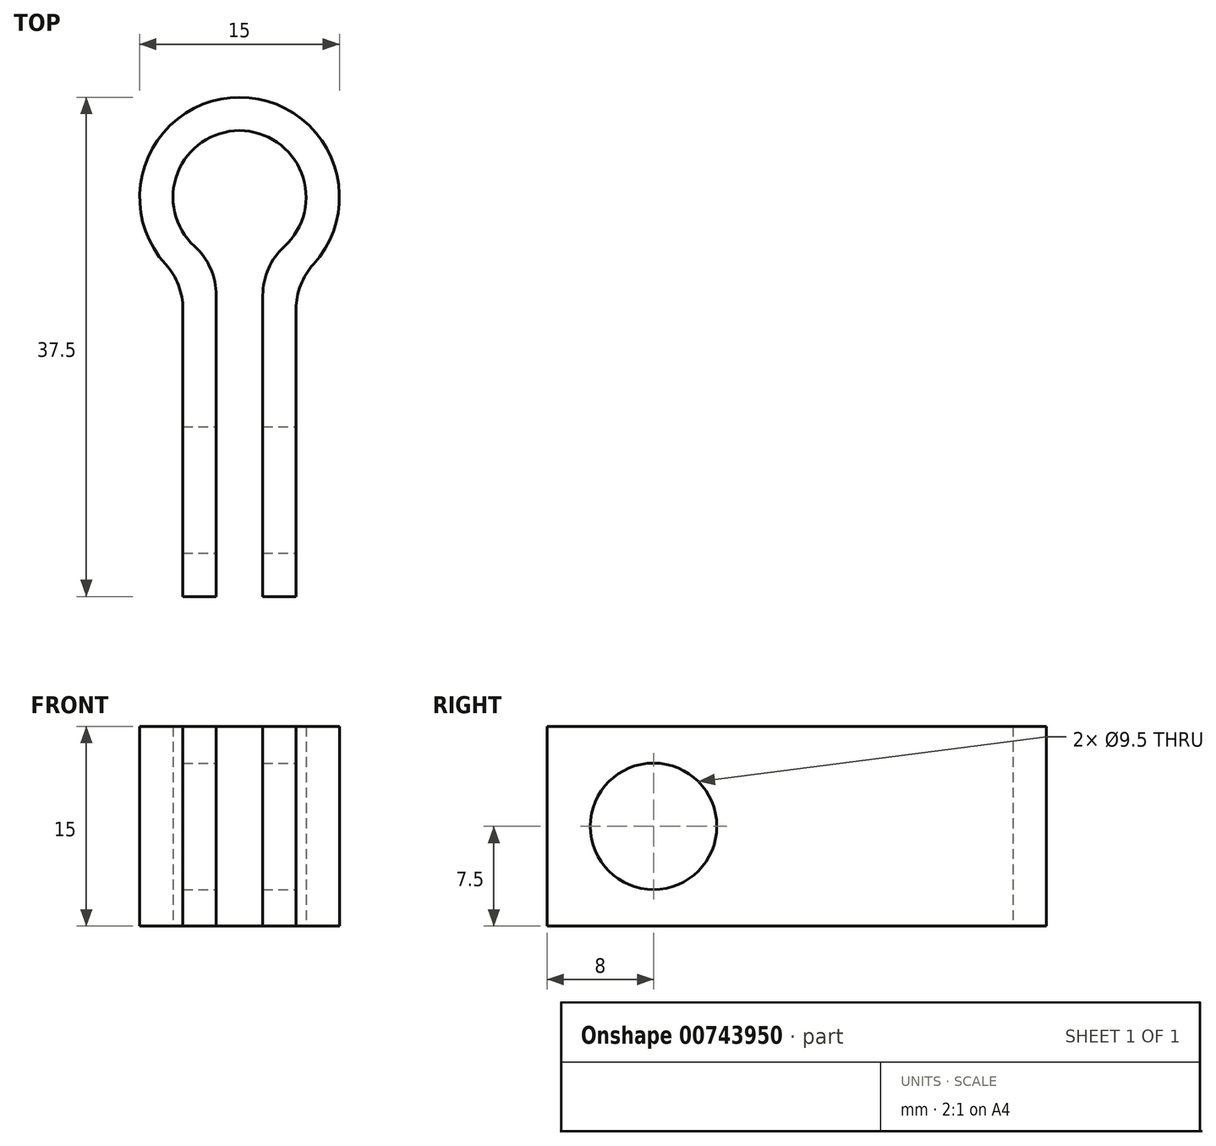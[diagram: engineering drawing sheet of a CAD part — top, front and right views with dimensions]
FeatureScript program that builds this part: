
annotation { "Feature Type Name" : "Feature", "Feature Type Description" : "" }
export const myFeature = defineFeature(function(context is Context, id is Id, definition is map)
    precondition{}
    {
        {
            var Q0;
            Q0=qCreatedBy(makeId("Top.planeOp"),FACE);
            var sketch = newSketch(context, id + "F0", { "sketchPlane" : qUnion([Q0])});
            skLineSegment(sketch, "E0", {"start": v(0, 15.33) * mm, "end": v(0, -22.93) * mm, "construction": true});
            skArc(sketch, "E1", {"start": v(3.38, -3.69) * mm, "mid": v(0, 5) * mm, "end": v(-3.38, -3.69) * mm});
            skLineSegment(sketch, "E2", {"start": v(-1.75, -7.38) * mm, "end": v(-1.75, -30) * mm});
            skLineSegment(sketch, "E3", {"start": v(-1.75, -30) * mm, "end": v(-4.25, -30) * mm});
            skLineSegment(sketch, "E4", {"start": v(-4.25, -30) * mm, "end": v(-4.25, -8.4) * mm});
            skLineSegment(sketch, "E5.MirrorCS", {"start": v(4.25, -30) * mm, "end": v(4.25, -8.4) * mm});
            skLineSegment(sketch, "E6.MirrorCS", {"start": v(1.75, -30) * mm, "end": v(4.25, -30) * mm});
            skLineSegment(sketch, "E7.MirrorCS", {"start": v(1.75, -7.38) * mm, "end": v(1.75, -30) * mm});
            skArc(sketch, "E8.trimOffspring", {"start": v(5.55, -5.04) * mm, "mid": v(0, 7.5) * mm, "end": v(-5.55, -5.04) * mm});
            skLineSegment(sketch, "E9", {"start": v(-9.49, 0) * mm, "end": v(8.76, 0) * mm, "construction": true});
            skPoint(sketch, "E10.visualSharp", {"position": v(4.25, -6.18) * mm});
            skArc(sketch, "E10.filletArc", {"start": v(5.55, -5.04) * mm, "mid": v(4.59, -6.6) * mm, "end": v(4.25, -8.4) * mm});
            skPoint(sketch, "E11.visualSharp", {"position": v(-4.25, -6.18) * mm});
            skArc(sketch, "E11.filletArc", {"start": v(-4.25, -8.4) * mm, "mid": v(-4.59, -6.6) * mm, "end": v(-5.55, -5.04) * mm});
            skPoint(sketch, "E12.visualSharp", {"position": v(-1.75, -4.68) * mm});
            skArc(sketch, "E12.filletArc", {"start": v(-1.75, -7.38) * mm, "mid": v(-2.17, -5.36) * mm, "end": v(-3.38, -3.69) * mm});
            skPoint(sketch, "E13.visualSharp", {"position": v(1.75, -4.68) * mm});
            skArc(sketch, "E13.filletArc", {"start": v(3.38, -3.69) * mm, "mid": v(2.17, -5.36) * mm, "end": v(1.75, -7.38) * mm});
            skSolve(sketch);
        }
        {
            var Q0;
            Q0=makeQuery(id+"F0.imprint","IMPRINT",FACE,{"disambiguationData":[TD([[makeQuery(id+"F0.imprint","IMPRINT",EDGE,{"derivedFrom":sQuery(id+"F0.wireOp",EDGE,"E1")}),-1.0]])]});
            extrude(context, id + "F1", {"entities" : qUnion([Q0]), "depth" : 15 * mm, "offsetDistance" : 25 * mm});
        }
        {
            var Q0;
            Q0=makeQuery(id+"F1.opExtrude","SWEPT_FACE",FACE,{"disambiguationData":[OSD([sQuery(id+"F0.wireOp",EDGE,"E5.MirrorCS")])]});
            var sketch = newSketch(context, id + "F2", { "sketchPlane" : qUnion([Q0])});
            skLineSegment(sketch, "E14", {"start": v(-30, 7.5) * mm, "end": v(-8.4, 7.5) * mm, "construction": true});
            skLineSegment(sketch, "E15", {"start": v(-22, 15) * mm, "end": v(-22, 0) * mm, "construction": true});
            skPoint(sketch, "E15.endSnap0", {"position": v(-19.2, 0) * mm});
            skPoint(sketch, "E16", {"position": v(-22, 7.5) * mm});
            skSolve(sketch);
        }
        {
            var Q0;
            Q0=sQuery(id+"F2.wireOp",VERTEX,"E16");
            var Q1;
            Q1=makeQuery(id+"F1.opExtrude","SWEPT_BODY",BODY,{"disambiguationData":[OSD([sQuery(id+"F0.wireOp",EDGE,"E1"),sQuery(id+"F0.wireOp",EDGE,"E2"),sQuery(id+"F0.wireOp",EDGE,"E3"),sQuery(id+"F0.wireOp",EDGE,"E4"),sQuery(id+"F0.wireOp",EDGE,"E5.MirrorCS"),sQuery(id+"F0.wireOp",EDGE,"E6.MirrorCS"),sQuery(id+"F0.wireOp",EDGE,"E7.MirrorCS"),sQuery(id+"F0.wireOp",EDGE,"E8.trimOffspring"),sQuery(id+"F0.wireOp",EDGE,"E10.filletArc"),sQuery(id+"F0.wireOp",EDGE,"E11.filletArc"),sQuery(id+"F0.wireOp",EDGE,"E12.filletArc"),sQuery(id+"F0.wireOp",EDGE,"E13.filletArc")])]});
            hole(context, id + "F3", {"style" : HoleStyle.SIMPLE, "endStyle" : HoleEndStyle.THROUGH, "holeDiameter" : 9.5 * mm, "majorDiameter" : 5 * mm, "isTappedThrough" : true, "tappedDepth" : 12 * mm, "tapClearance" : 3, "startFromSketch" : true, "locations" : qUnion([Q0]), "scope" : qUnion([Q1])});
        }
    });
